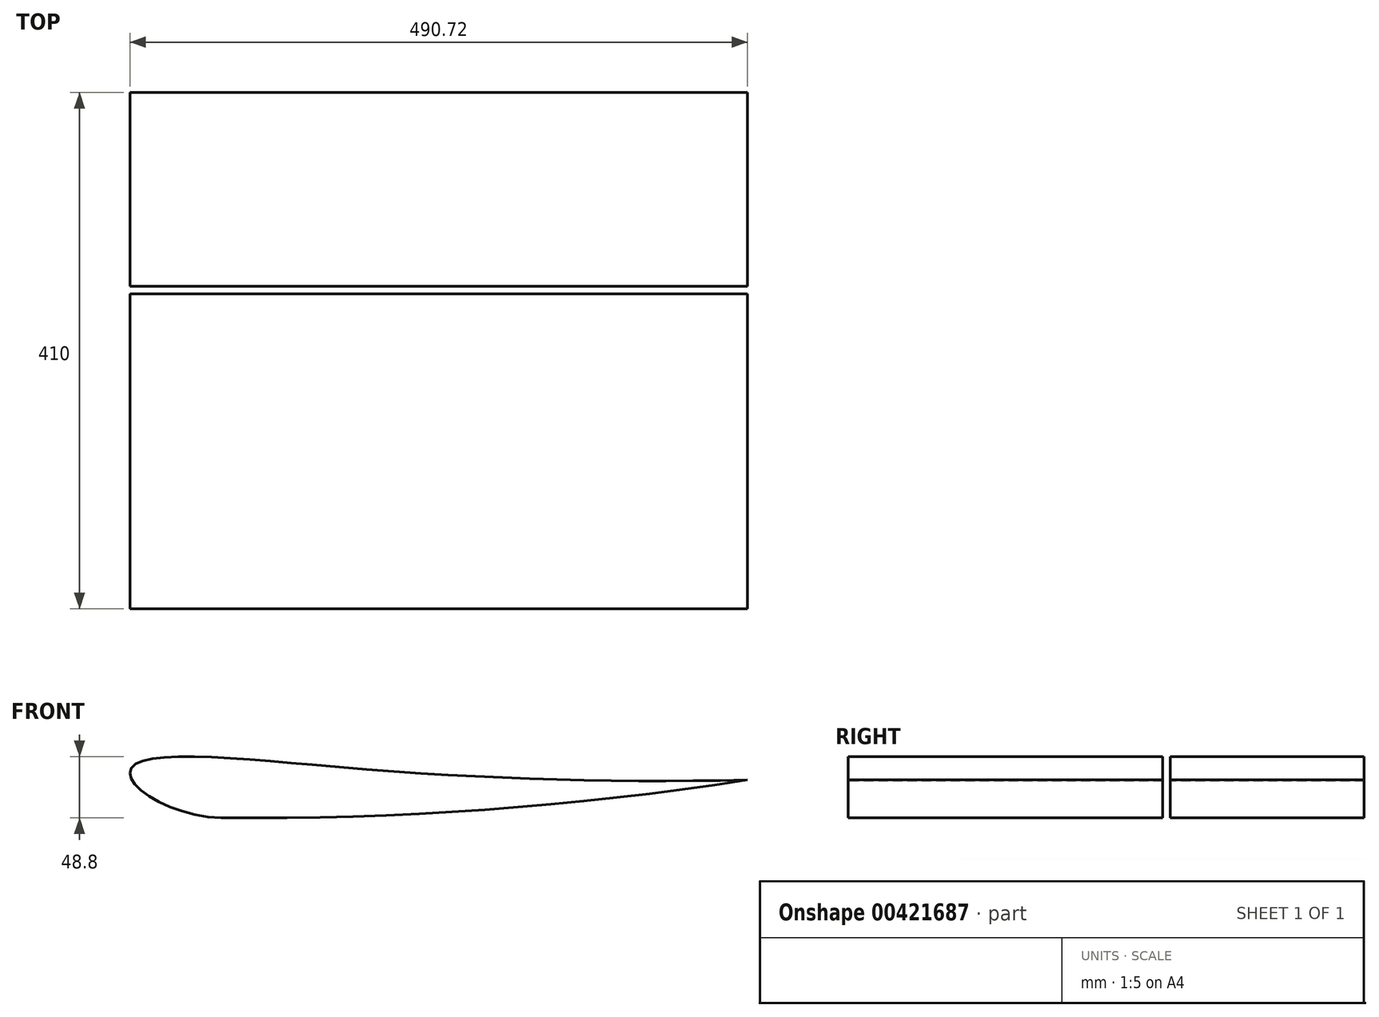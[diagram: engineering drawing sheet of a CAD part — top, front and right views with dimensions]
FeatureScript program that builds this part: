
annotation { "Feature Type Name" : "Feature", "Feature Type Description" : "" }
export const myFeature = defineFeature(function(context is Context, id is Id, definition is map)
    precondition{}
    {
        {
            var Q0;
            Q0=qCreatedBy(makeId("Front.planeOp"),FACE);
            cPlane(context, id + "F0", {"entities" : qUnion([Q0]), "cplaneType" : CPlaneType.OFFSET, "offset" : 253 * mm, "oppositeDirection" : true, "width" : 150 * mm, "height" : 150 * mm});
        }
        {
            var Q0;
            Q0=qCreatedBy(id+"F0.planeOp",FACE);
            var sketch = newSketch(context, id + "F1", { "sketchPlane" : qUnion([Q0])});
            skPoint(sketch, "E0", {"position": v(-988.72, 148.42) * mm});
            skPoint(sketch, "E1", {"position": v(-1334.5, 160.44) * mm});
            skPoint(sketch, "E2", {"position": v(-1475.94, 145.57) * mm});
            skPoint(sketch, "E3", {"position": v(-1475.94, 160.44) * mm});
            skArc(sketch, "E4", {"start": v(-1334.5, 160.44) * mm, "mid": v(-1161.78, 149.44) * mm, "end": v(-988.72, 148.42) * mm});
            skFitSpline(sketch, "E5", {"points": [v(-1334.5, 160.44) * mm, v(-1475.94, 160.44) * mm, v(-1475.94, 145.57) * mm, v(-1406.93, 118.4) * mm], "startDerivative": vector(-384.1, 35.63) * mm, "endDerivative": vector(239.27, -2.63) * mm});
            skArc(sketch, "E6", {"start": v(-1406.93, 118.4) * mm, "mid": v(-1197.2, 124.76) * mm, "end": v(-988.72, 148.42) * mm});
            skSolve(sketch);
        }
        {
            var Q0;
            Q0=makeQuery(id+"F1.imprint","IMPRINT",FACE,{"disambiguationData":[TD([[makeQuery(id+"F1.imprint","IMPRINT",EDGE,{"derivedFrom":sQuery(id+"F1.wireOp",EDGE,"E4")}),-1.0]])]});
            extrude(context, id + "F2", {"entities" : qUnion([Q0]), "oppositeDirection" : true, "depth" : 410 * mm});
        }
        {
            var Q0;
            Q0=qCreatedBy(makeId("Top.planeOp"),FACE);
            var sketch = newSketch(context, id + "F3", { "sketchPlane" : qUnion([Q0])});
            skPoint(sketch, "E7", {"position": v(-151.04, 503) * mm});
            skLineSegment(sketch, "E8.bottom", {"start": v(-151.04, 503) * mm, "end": v(-1710.38, 503) * mm});
            skLineSegment(sketch, "E8.top", {"start": v(-151.04, 509) * mm, "end": v(-1710.38, 509) * mm});
            skLineSegment(sketch, "E8.left", {"start": v(-151.04, 503) * mm, "end": v(-151.04, 509) * mm});
            skLineSegment(sketch, "E8.right", {"start": v(-1710.38, 503) * mm, "end": v(-1710.38, 509) * mm});
            skSolve(sketch);
        }
        {
            var Q0;
            Q0=makeQuery(id+"F3.imprint","IMPRINT",FACE,{"disambiguationData":[TD([[makeQuery(id+"F3.imprint","IMPRINT",EDGE,{"derivedFrom":sQuery(id+"F3.wireOp",EDGE,"E8.bottom")}),-1.0]])]});
            extrude(context, id + "F4", {"entities" : qUnion([Q0]), "operationType" : NewBodyOperationType.REMOVE, "endBound" : BoundingType.THROUGH_ALL, "depth" : 25 * mm});
        }
    });
